# Revit family: Sanitary_Installation-Systems_AXOR_35363USA-AXOR-ShowerSolutions-Basic-set-for-overhead-shower-ceiling
name_source: partatom
category: Plumbing Fixtures
revit_build: Autodesk Revit 2018 (Build: 20190510_1515(x64)
units: mm (PartAtom-declared; Revit-internal decimal feet)

## family parameters
Always vertical = No
Cut with Voids When Loaded = No
OmniClass Number = 23.27.31.29.11
OmniClass Title = Manual Mixing Valves
Part Type = Normal
Room Calculation Point = No
Round Connector Dimension = Use Diameter
Shared = No
Work Plane-Based = Yes

## types (1)
- 35363USA AXOR ShowerSolutions Basic set for overhead shower ceiling
    Always visible = Yes
    BIMobject category = Installation Systems
    Connector Description = Water Inlet 21,336 mm
    Default Elevation = 1219.2 mm  [stored 4 ft]
    Description = AXOR ShowerSolutions Basic set for overhead shower ceiling
    Diameter = 21 mm
    Edition number = 1
    IFC Classification = Sanitary Terminal
    Main Material = Axor - Metal - Chrome
    Manufacturer = AXOR
    Manufacturer name = AXOR
    Model = 35363USA AXOR ShowerSolutions Basic set for overhead shower ceiling
    OmniClass Code = 23-27 31 29 11
    OmniClass Description = Manual Mixing Valves
    Product Guid = 38ca97b0-2589-4bb2-8d9f-a4038b801bb8
    Product SKU = 35363USA
    Product data url = https://bimobject.com
    Product family = AXOR ShowerSolutions
    Product group = Basic set shower
    Product name = 35363USA AXOR ShowerSolutions Basic set for overhead shower ceiling
    Product url = https://www.axor-design.com
    QR code = https://bimobject.com
    Secondary Material = Axor - Plastic - Matt White
    URL = https://www.axor-design.com
    Weight Net (Kg) = 0,8

note: [stored X ft] marks values corroborated as IEEE doubles in the binary element streams (Revit-internal decimal feet)

## geometry (parser evidence)
native form markers: Sweep x2
no freeform markers — native parametric forms only
